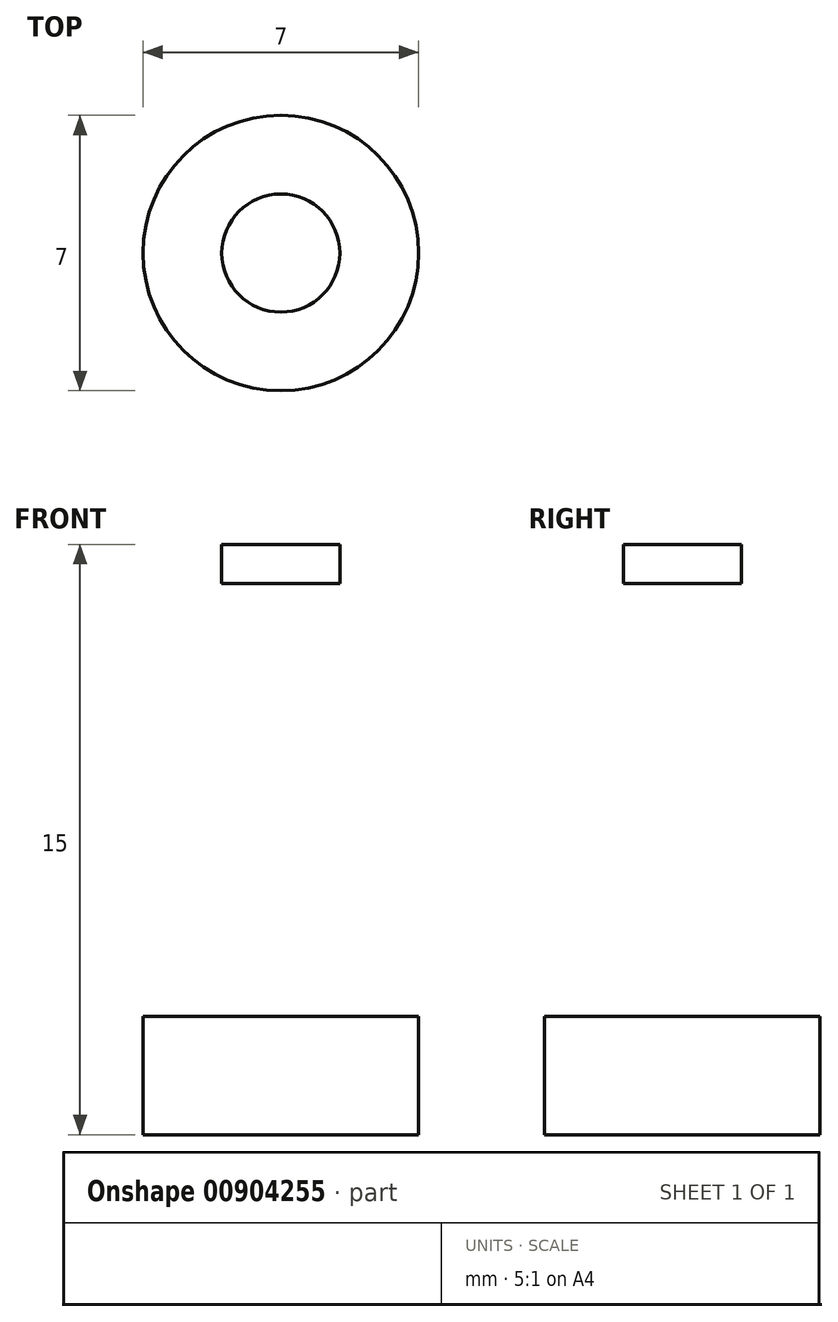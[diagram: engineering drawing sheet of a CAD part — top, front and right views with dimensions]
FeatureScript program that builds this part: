
annotation { "Feature Type Name" : "Feature", "Feature Type Description" : "" }
export const myFeature = defineFeature(function(context is Context, id is Id, definition is map)
    precondition{}
    {
        {
            var Q0;
            Q0=qCreatedBy(makeId("Front.planeOp"),FACE);
            var sketch = newSketch(context, id + "F0", { "sketchPlane" : qUnion([Q0])});
            skLineSegment(sketch, "E0.bottom", {"start": v(0, 0) * mm, "end": v(-3.5, 0) * mm});
            skLineSegment(sketch, "E0.top", {"start": v(0, 3) * mm, "end": v(-3.5, 3) * mm});
            skLineSegment(sketch, "E0.left", {"start": v(0, 0) * mm, "end": v(0, 3) * mm});
            skLineSegment(sketch, "E0.right", {"start": v(-3.5, 0) * mm, "end": v(-3.5, 3) * mm});
            skLineSegment(sketch, "E1.bottom", {"start": v(0, 3) * mm, "end": v(-1, 3) * mm});
            skLineSegment(sketch, "E1.top", {"start": v(0, 14) * mm, "end": v(-1, 14) * mm});
            skLineSegment(sketch, "E1.left", {"start": v(0, 3) * mm, "end": v(0, 14) * mm});
            skLineSegment(sketch, "E1.right", {"start": v(-1, 3) * mm, "end": v(-1, 14) * mm});
            skLineSegment(sketch, "E2.bottom", {"start": v(0, 14) * mm, "end": v(-1.5, 14) * mm});
            skLineSegment(sketch, "E2.top", {"start": v(0, 15) * mm, "end": v(-1.5, 15) * mm});
            skLineSegment(sketch, "E2.left", {"start": v(0, 14) * mm, "end": v(0, 15) * mm});
            skLineSegment(sketch, "E2.right", {"start": v(-1.5, 14) * mm, "end": v(-1.5, 15) * mm});
            skSolve(sketch);
        }
        {
            var Q0;
            Q0=makeQuery(id+"F0.imprint","IMPRINT",FACE,{"disambiguationData":[TD([[makeQuery(id+"F0.imprint","IMPRINT",EDGE,{"derivedFrom":sQuery(id+"F0.wireOp",EDGE,"E0.bottom")}),-1.0]])]});
            var Q1;
            Q1=makeQuery(id+"F0.imprint","IMPRINT",FACE,{"disambiguationData":[TD([[makeQuery(id+"F0.imprint","IMPRINT",EDGE,{"derivedFrom":sQuery(id+"F0.wireOp",EDGE,"E1.bottom")}),-1.0]])]});
            var Q2;
            Q2=makeQuery(id+"F0.imprint","IMPRINT",FACE,{"disambiguationData":[TD([[makeQuery(id+"F0.imprint","IMPRINT",EDGE,{"derivedFrom":sQuery(id+"F0.wireOp",EDGE,"E2.top")}),1.0]])]});
            var Q3;
            Q3=sQuery(id+"F0.wireOp",EDGE,"E1.left");
            revolve(context, id + "F1", {"surfaceOperationType" : NewSurfaceOperationType.NEW, "entities" : qUnion([Q0, Q1, Q2]), "axis" : qUnion([Q3]), "revolveType" : RevolveType.FULL});
        }
    });
